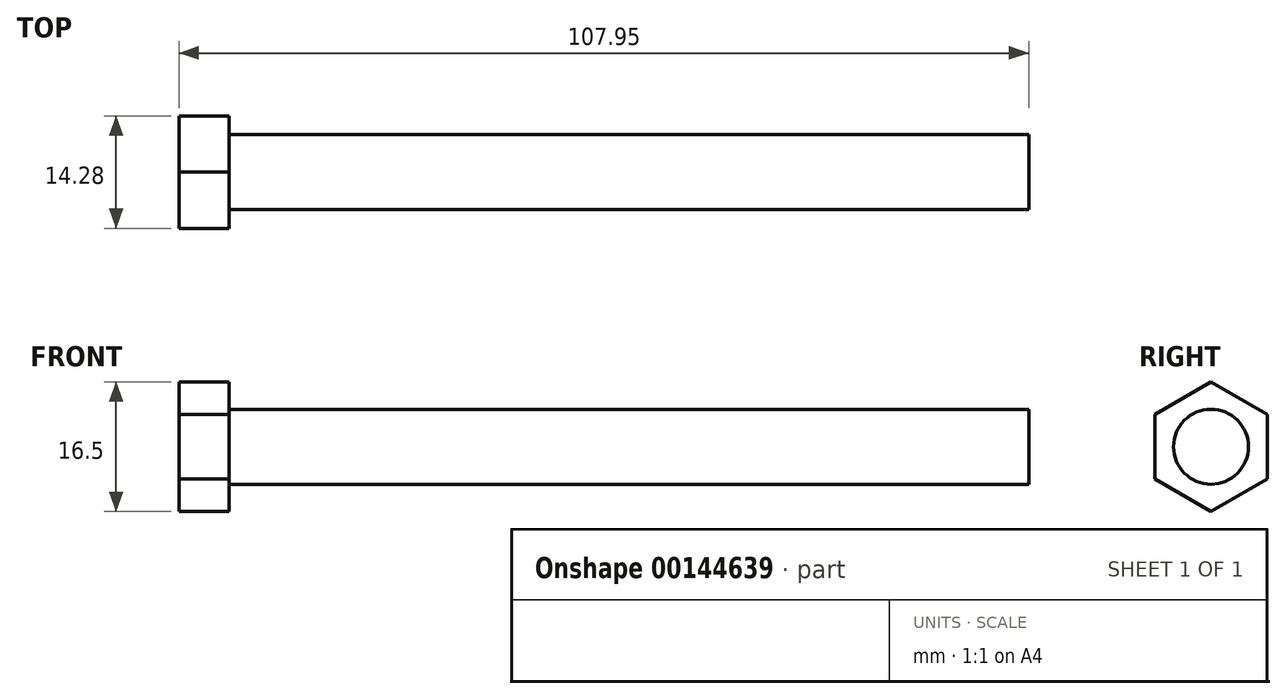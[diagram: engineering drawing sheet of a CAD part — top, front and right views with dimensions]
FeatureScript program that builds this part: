
annotation { "Feature Type Name" : "Feature", "Feature Type Description" : "" }
export const myFeature = defineFeature(function(context is Context, id is Id, definition is map)
    precondition{}
    {
        {
            var Q0;
            Q0=qCreatedBy(makeId("Right.planeOp"),FACE);
            var sketch = newSketch(context, id + "F0", { "sketchPlane" : qUnion([Q0])});
            skCircle(sketch, "E0.cCircle", {"center": v(0, 0) * mm, "radius": 7.14 * mm, "construction": true});
            skLineSegment(sketch, "E0.0", {"start": v(7.14, 4.12) * mm, "end": v(7.14, -4.12) * mm});
            skLineSegment(sketch, "E0.1", {"start": v(7.14, -4.12) * mm, "end": v(0, -8.25) * mm});
            skLineSegment(sketch, "E0.2", {"start": v(0, -8.25) * mm, "end": v(-7.14, -4.12) * mm});
            skLineSegment(sketch, "E0.3", {"start": v(-7.14, -4.12) * mm, "end": v(-7.14, 4.12) * mm});
            skLineSegment(sketch, "E0.4", {"start": v(-7.14, 4.12) * mm, "end": v(0, 8.25) * mm});
            skLineSegment(sketch, "E0.5", {"start": v(0, 8.25) * mm, "end": v(7.14, 4.12) * mm});
            skPoint(sketch, "E0.0.midPoint", {"position": v(7.14, 0) * mm});
            skCircle(sketch, "E1", {"center": v(0, 0) * mm, "radius": 4.76 * mm});
            skSolve(sketch);
        }
        {
            var Q0;
            Q0=makeQuery(id+"F0.imprint","IMPRINT",FACE,{"disambiguationData":[TD([[makeQuery(id+"F0.imprint","IMPRINT",EDGE,{"derivedFrom":sQuery(id+"F0.wireOp",EDGE,"E0.0")}),-1.0]])]});
            var Q1;
            Q1=makeQuery(id+"F0.imprint","IMPRINT",FACE,{"disambiguationData":[TD([[makeQuery(id+"F0.imprint","IMPRINT",EDGE,{"derivedFrom":sQuery(id+"F0.wireOp",EDGE,"E1")}),1.0]])]});
            extrude(context, id + "F1", {"entities" : qUnion([Q0, Q1]), "oppositeDirection" : true, "depth" : 6.35 * mm});
        }
        {
            var Q0;
            Q0=makeQuery(id+"F0.imprint","IMPRINT",FACE,{"disambiguationData":[TD([[makeQuery(id+"F0.imprint","IMPRINT",EDGE,{"derivedFrom":sQuery(id+"F0.wireOp",EDGE,"E1")}),1.0]])]});
            extrude(context, id + "F2", {"entities" : qUnion([Q0]), "operationType" : NewBodyOperationType.ADD, "depth" : 101.6 * mm});
        }
    });
